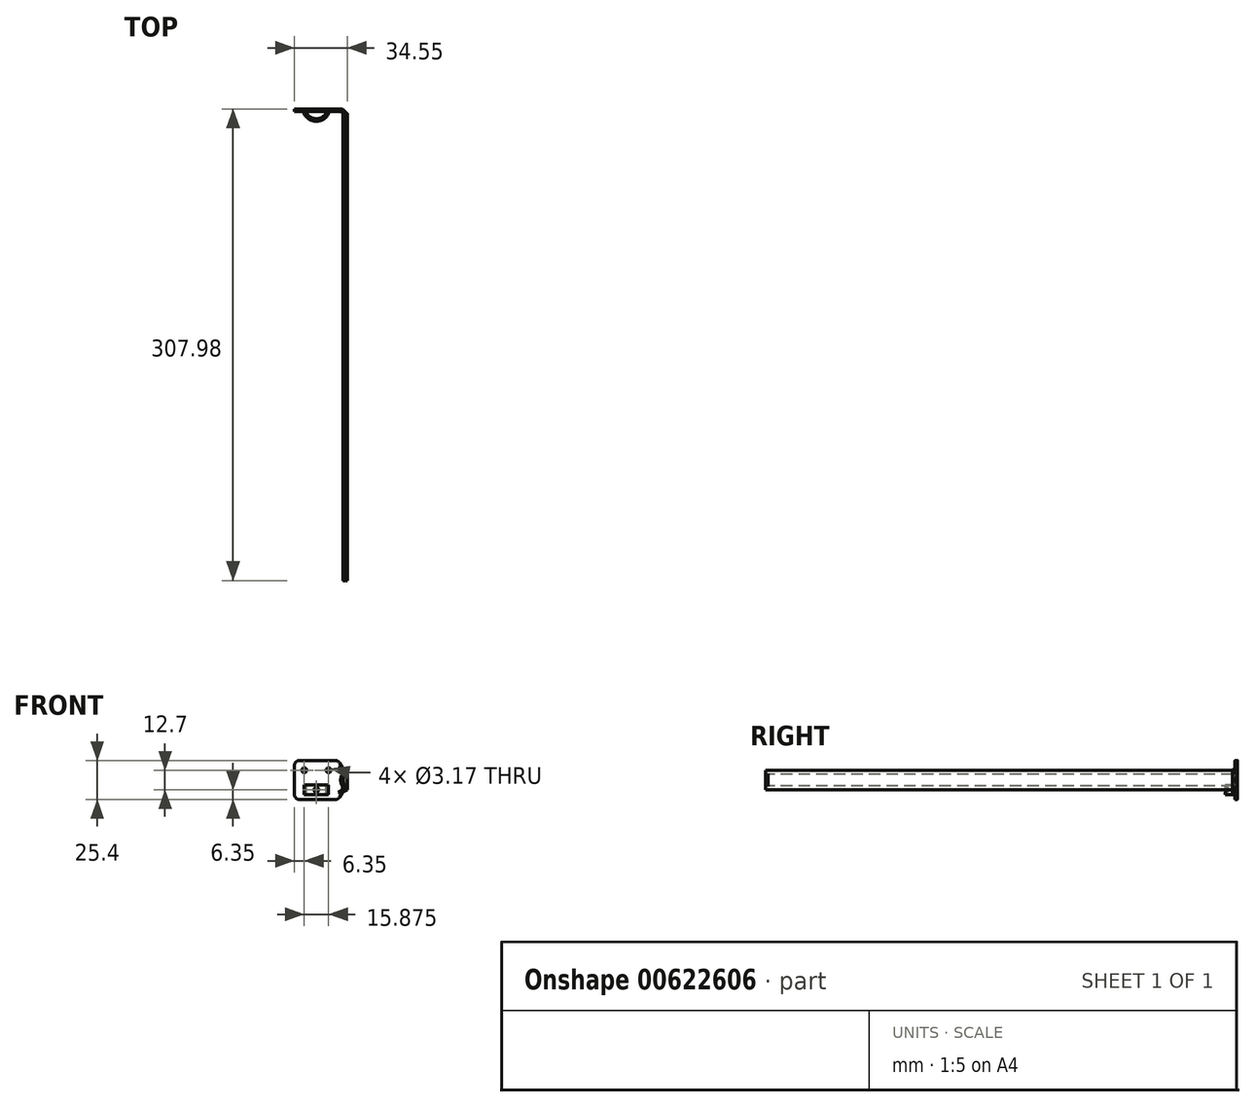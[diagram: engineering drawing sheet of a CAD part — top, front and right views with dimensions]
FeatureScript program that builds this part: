
annotation { "Feature Type Name" : "Feature", "Feature Type Description" : "" }
export const myFeature = defineFeature(function(context is Context, id is Id, definition is map)
    precondition{}
    {
        {
            var Q0;
            Q0=qCreatedBy(makeId("Front.planeOp"),FACE);
            var sketch = newSketch(context, id + "F0", { "sketchPlane" : qUnion([Q0])});
            skLineSegment(sketch, "E0", {"start": v(0, 6.35) * mm, "end": v(0, 4.22) * mm});
            skLineSegment(sketch, "E1", {"start": v(0, -6.35) * mm, "end": v(0, -4.22) * mm});
            skArc(sketch, "E2", {"start": v(-0.49, 2.53) * mm, "mid": v(-1.21, 0) * mm, "end": v(-0.49, -2.53) * mm});
            skPoint(sketch, "E3.visualSharp", {"position": v(0, 3.17) * mm});
            skArc(sketch, "E3.filletArc", {"start": v(-0.49, 2.53) * mm, "mid": v(-0.12, 3.34) * mm, "end": v(0, 4.22) * mm});
            skPoint(sketch, "E4.visualSharp", {"position": v(0, -3.18) * mm});
            skArc(sketch, "E4.filletArc", {"start": v(0, -4.22) * mm, "mid": v(-0.12, -3.34) * mm, "end": v(-0.49, -2.53) * mm});
            skLineSegment(sketch, "E5.0", {"start": v(-1.59, -6.35) * mm, "end": v(-1.59, -3.73) * mm});
            skArc(sketch, "E5.1", {"start": v(-1.59, 3.73) * mm, "mid": v(-2.8, 0) * mm, "end": v(-1.59, -3.73) * mm});
            skLineSegment(sketch, "E5.2", {"start": v(-1.59, 6.35) * mm, "end": v(-1.59, 3.73) * mm});
            skLineSegment(sketch, "E6", {"start": v(-1.59, 6.35) * mm, "end": v(0, 6.35) * mm});
            skLineSegment(sketch, "E7", {"start": v(-1.59, -6.35) * mm, "end": v(0, -6.35) * mm});
            skSolve(sketch);
        }
        {
            var Q0;
            Q0=qSketchRegion(id+"F0",true);
            extrude(context, id + "F1", {"entities" : qUnion([Q0]), "oppositeDirection" : true, "depth" : 304.8 * mm, "offsetDistance" : 25.4 * mm});
        }
        {
            var Q0;
            Q0=makeQuery(id+"F1.opExtrude","CAP_FACE",FACE,{"disambiguationData":[OSD([sQuery(id+"F0.wireOp",EDGE,"E0"),sQuery(id+"F0.wireOp",EDGE,"E1"),sQuery(id+"F0.wireOp",EDGE,"E2"),sQuery(id+"F0.wireOp",EDGE,"E3.filletArc"),sQuery(id+"F0.wireOp",EDGE,"E4.filletArc"),sQuery(id+"F0.wireOp",EDGE,"E5.0"),sQuery(id+"F0.wireOp",EDGE,"E5.1"),sQuery(id+"F0.wireOp",EDGE,"E5.2"),sQuery(id+"F0.wireOp",EDGE,"E6"),sQuery(id+"F0.wireOp",EDGE,"E7")])],"isStart":false});
            cPlane(context, id + "F2", {"entities" : qUnion([Q0]), "cplaneType" : CPlaneType.OFFSET, "offset" : 3.17 * mm, "width" : 152.4 * mm, "height" : 152.4 * mm});
        }
        {
            var Q0;
            Q0=qCreatedBy(id+"F2.planeOp",FACE);
            var sketch = newSketch(context, id + "F3", { "sketchPlane" : qUnion([Q0])});
            skLineSegment(sketch, "E8.0", {"start": v(4.76, -6.35) * mm, "end": v(4.76, -4.65) * mm});
            skArc(sketch, "E8.1", {"start": v(4.76, 4.65) * mm, "mid": v(5.98, 0) * mm, "end": v(4.76, -4.65) * mm});
            skLineSegment(sketch, "E8.2", {"start": v(4.76, 6.35) * mm, "end": v(4.76, 4.65) * mm});
            skLineSegment(sketch, "E9.0", {"start": v(3.18, -6.35) * mm, "end": v(3.18, -5.05) * mm});
            skArc(sketch, "E9.1", {"start": v(3.52, 3.6) * mm, "mid": v(4.39, 0) * mm, "end": v(3.52, -3.6) * mm});
            skLineSegment(sketch, "E9.2", {"start": v(3.18, 6.35) * mm, "end": v(3.18, 5.05) * mm});
            skLineSegment(sketch, "E10", {"start": v(3.18, 6.35) * mm, "end": v(4.76, 6.35) * mm});
            skLineSegment(sketch, "E11", {"start": v(3.18, -6.35) * mm, "end": v(4.76, -6.35) * mm});
            skPoint(sketch, "E12.visualSharp", {"position": v(3.18, 4.22) * mm});
            skArc(sketch, "E12.filletArc", {"start": v(3.18, 5.05) * mm, "mid": v(3.26, 4.3) * mm, "end": v(3.52, 3.6) * mm});
            skPoint(sketch, "E13.visualSharp", {"position": v(3.18, -4.22) * mm});
            skArc(sketch, "E13.filletArc", {"start": v(3.52, -3.6) * mm, "mid": v(3.26, -4.3) * mm, "end": v(3.18, -5.05) * mm});
            skLineSegment(sketch, "E14", {"start": v(5.98, 0) * mm, "end": v(5.98, 6.46) * mm, "construction": true});
            skLineSegment(sketch, "E15", {"start": v(5.98, 0) * mm, "end": v(5.98, -6.35) * mm, "construction": true});
            skSolve(sketch);
        }
        {
            var Q1;
            Q1=makeQuery(id+"F1.opExtrude","CAP_FACE",FACE,{"disambiguationData":[OSD([sQuery(id+"F0.wireOp",EDGE,"E0"),sQuery(id+"F0.wireOp",EDGE,"E1"),sQuery(id+"F0.wireOp",EDGE,"E2"),sQuery(id+"F0.wireOp",EDGE,"E3.filletArc"),sQuery(id+"F0.wireOp",EDGE,"E4.filletArc"),sQuery(id+"F0.wireOp",EDGE,"E5.0"),sQuery(id+"F0.wireOp",EDGE,"E5.1"),sQuery(id+"F0.wireOp",EDGE,"E5.2"),sQuery(id+"F0.wireOp",EDGE,"E6"),sQuery(id+"F0.wireOp",EDGE,"E7")])],"isStart":false});
            var Q2;
            Q2=makeQuery(id+"F3.imprint","IMPRINT",FACE,{"disambiguationData":[TD([[makeQuery(id+"F3.imprint","IMPRINT",EDGE,{"derivedFrom":sQuery(id+"F3.wireOp",EDGE,"E8.0")}),1.0]])]});
            loft(context, id + "F4", {"operationType" : NewBodyOperationType.ADD, "sheetProfilesArray" : [{ "sheetProfileEntities" : qUnion([Q1]) }, { "sheetProfileEntities" : qUnion([Q2]) }]});
        }
        {
            var Q0;
            Q0=makeQuery(id+"F4.opLoft","CAP_FACE",FACE,{"disambiguationData":[OSD([makeQuery(id+"F3.imprint","IMPRINT",FACE,{"disambiguationData":[TD([[makeQuery(id+"F3.imprint","IMPRINT",EDGE,{"derivedFrom":sQuery(id+"F3.wireOp",EDGE,"E8.0")}),1.0]])]})])],"isStart":true});
            cPlane(context, id + "F5", {"entities" : qUnion([Q0]), "cplaneType" : CPlaneType.OFFSET, "offset" : 0 * mm, "width" : 152.4 * mm, "height" : 152.4 * mm});
        }
        {
            var Q0;
            Q0=qCreatedBy(id+"F5.planeOp",FACE);
            var sketch = newSketch(context, id + "F6", { "sketchPlane" : qUnion([Q0])});
            skLineSegment(sketch, "E16.bottom", {"start": v(3.17, -7.94) * mm, "end": v(5.98, -7.94) * mm});
            skLineSegment(sketch, "E16.top", {"start": v(3.18, 7.94) * mm, "end": v(5.98, 7.94) * mm});
            skLineSegment(sketch, "E16.left", {"start": v(3.18, -7.94) * mm, "end": v(3.18, 7.94) * mm});
            skLineSegment(sketch, "E16.right", {"start": v(5.98, -7.94) * mm, "end": v(5.98, 7.94) * mm});
            skPoint(sketch, "E16.middle", {"position": v(4.58, 0) * mm});
            skLineSegment(sketch, "E17", {"start": v(4.58, 7.94) * mm, "end": v(4.58, -7.94) * mm, "construction": true});
            skSolve(sketch);
        }
        {
            var Q0;
            Q0=qSketchRegion(id+"F6",true);
            extrude(context, id + "F7", {"entities" : qUnion([Q0]), "operationType" : NewBodyOperationType.ADD, "oppositeDirection" : true, "depth" : 1.59 * mm, "offsetDistance" : 25.4 * mm});
        }
        {
            var Q0;
            {var subQ0=sQuery(id+"F0.wireOp",EDGE,"E6");Q0=makeQuery(id+"F4.boolean.opBoolean","MERGE",FACE,{"derivedFrom":[makeQuery(id+"F1.opExtrude","SWEPT_FACE",FACE,{"disambiguationData":[OSD([subQ0])]}),makeQuery(id+"F4.opLoft","SWEPT_FACE",FACE,{"disambiguationData":[OSD([sQuery(id+"F0.wireOp",EDGE,"E0"),sQuery(id+"F0.wireOp",EDGE,"E5.2"),subQ0,sQuery(id+"F3.wireOp",EDGE,"E8.2"),sQuery(id+"F3.wireOp",EDGE,"E9.2"),sQuery(id+"F3.wireOp",EDGE,"E10")])]})]});}
            var sketch = newSketch(context, id + "F8", { "sketchPlane" : qUnion([Q0])});
            skLineSegment(sketch, "E18", {"start": v(-1.59, 304.8) * mm, "end": v(0, 304.8) * mm});
            skSolve(sketch);
        }
        {
            var Q1;
            Q1=makeQuery(id+"F7.opExtrude","SWEPT_FACE",FACE,{"disambiguationData":[OSD([sQuery(id+"F6.wireOp",EDGE,"E16.top")])]});
            var Q2;
            Q2=makeQuery(id+"F8.imprint","IMPRINT",FACE,{"disambiguationData":[TD([[makeQuery(id+"F8.imprint","IMPRINT",EDGE,{"derivedFrom":sQuery(id+"F8.wireOp",EDGE,"E18")}),1.0]])]});
            loft(context, id + "F9", {"operationType" : NewBodyOperationType.ADD, "sheetProfilesArray" : [{ "sheetProfileEntities" : qUnion([Q1]) }, { "sheetProfileEntities" : qUnion([Q2]) }]});
        }
        {
            var Q0;
            {var subQ0=sQuery(id+"F0.wireOp",EDGE,"E7");Q0=makeQuery(id+"F4.boolean.opBoolean","MERGE",FACE,{"derivedFrom":[makeQuery(id+"F1.opExtrude","SWEPT_FACE",FACE,{"disambiguationData":[OSD([subQ0])]}),makeQuery(id+"F4.opLoft","SWEPT_FACE",FACE,{"disambiguationData":[OSD([sQuery(id+"F0.wireOp",EDGE,"E1"),sQuery(id+"F0.wireOp",EDGE,"E5.0"),subQ0,sQuery(id+"F3.wireOp",EDGE,"E8.0"),sQuery(id+"F3.wireOp",EDGE,"E9.0"),sQuery(id+"F3.wireOp",EDGE,"E11")])]})]});}
            var sketch = newSketch(context, id + "F10", { "sketchPlane" : qUnion([Q0])});
            skLineSegment(sketch, "E19", {"start": v(0, -304.8) * mm, "end": v(-1.59, -304.8) * mm});
            skSolve(sketch);
        }
        {
            var Q1;
            Q1=makeQuery(id+"F7.opExtrude","SWEPT_FACE",FACE,{"disambiguationData":[OSD([sQuery(id+"F6.wireOp",EDGE,"E16.bottom")])]});
            var Q2;
            Q2=makeQuery(id+"F10.imprint","IMPRINT",FACE,{"disambiguationData":[TD([[makeQuery(id+"F10.imprint","IMPRINT",EDGE,{"derivedFrom":sQuery(id+"F10.wireOp",EDGE,"E19")}),1.0]])]});
            loft(context, id + "F11", {"operationType" : NewBodyOperationType.ADD, "sheetProfilesArray" : [{ "sheetProfileEntities" : qUnion([Q1]) }, { "sheetProfileEntities" : qUnion([Q2]) }]});
        }
        {
            var Q0;
            Q0=makeQuery(id+"F7.opExtrude","SWEPT_FACE",FACE,{"disambiguationData":[OSD([sQuery(id+"F6.wireOp",EDGE,"E16.right")])]});
            var sketch = newSketch(context, id + "F12", { "sketchPlane" : qUnion([Q0])});
            skLineSegment(sketch, "E20.bottom", {"start": v(-307.98, -12.7) * mm, "end": v(-306.39, -12.7) * mm});
            skLineSegment(sketch, "E20.top", {"start": v(-307.98, 12.7) * mm, "end": v(-306.39, 12.7) * mm});
            skLineSegment(sketch, "E20.left", {"start": v(-307.98, -12.7) * mm, "end": v(-307.98, 12.7) * mm});
            skLineSegment(sketch, "E20.right", {"start": v(-306.39, -12.7) * mm, "end": v(-306.39, 12.7) * mm});
            skPoint(sketch, "E20.middle", {"position": v(-307.18, 0) * mm});
            skPoint(sketch, "E20.middle.positionSnap0", {"position": v(-307.18, 7.94) * mm});
            skPoint(sketch, "E20.middle.positionSnap1", {"position": v(-306.39, 0) * mm});
            skPoint(sketch, "E20.centerSnap0", {"position": v(-307.18, 7.94) * mm});
            skPoint(sketch, "E20.centerSnap1", {"position": v(-306.39, 0) * mm});
            skSolve(sketch);
        }
        {
            var Q0;
            Q0=qSketchRegion(id+"F12",true);
            extrude(context, id + "F13", {"entities" : qUnion([Q0]), "operationType" : NewBodyOperationType.ADD, "depth" : 28.57 * mm, "offsetDistance" : 25.4 * mm});
        }
        {
            var Q1;
            Q1=makeQuery(id+"F7.opExtrude","SWEPT_FACE",FACE,{"disambiguationData":[OSD([sQuery(id+"F6.wireOp",EDGE,"E16.top")])]});
            var Q2;
            Q2=makeQuery(id+"F13.opExtrude","SWEPT_FACE",FACE,{"disambiguationData":[OSD([sQuery(id+"F12.wireOp",EDGE,"E20.top")])]});
            loft(context, id + "F14", {"operationType" : NewBodyOperationType.ADD, "sheetProfilesArray" : [{ "sheetProfileEntities" : qUnion([Q1]) }, { "sheetProfileEntities" : qUnion([Q2]) }]});
        }
        {
            var Q1;
            Q1=makeQuery(id+"F7.opExtrude","SWEPT_FACE",FACE,{"disambiguationData":[OSD([sQuery(id+"F6.wireOp",EDGE,"E16.bottom")])]});
            var Q2;
            Q2=makeQuery(id+"F13.opExtrude","SWEPT_FACE",FACE,{"disambiguationData":[OSD([sQuery(id+"F12.wireOp",EDGE,"E20.bottom")])]});
            loft(context, id + "F15", {"operationType" : NewBodyOperationType.ADD, "sheetProfilesArray" : [{ "sheetProfileEntities" : qUnion([Q1]) }, { "sheetProfileEntities" : qUnion([Q2]) }]});
        }
        {
            var Q0;
            {var subQ0=sQuery(id+"F12.wireOp",EDGE,"E20.right");var subQ1=sQuery(id+"F6.wireOp",EDGE,"E16.right");var subQ2=sQuery(id+"F6.wireOp",EDGE,"E16.left");var subQ3=sQuery(id+"F6.wireOp",EDGE,"E16.bottom");var subQ4=sQuery(id+"F6.wireOp",EDGE,"E16.top");Q0=makeQuery(id+"F15.boolean.opBoolean","MERGE",FACE,{"derivedFrom":[makeQuery(id+"F14.boolean.opBoolean","MERGE",FACE,{"derivedFrom":[makeQuery(id+"F13.boolean.opBoolean","MERGE",FACE,{"derivedFrom":[makeQuery(id+"F7.opExtrude","CAP_FACE",FACE,{"disambiguationData":[OSD([subQ3,subQ4,subQ2,subQ1])],"isStart":false}),makeQuery(id+"F13.opExtrude","SWEPT_FACE",FACE,{"disambiguationData":[OSD([subQ0])]})]}),makeQuery(id+"F14.opLoft","SWEPT_FACE",FACE,{"disambiguationData":[OSD([subQ4,subQ2,subQ1,sQuery(id+"F12.wireOp",EDGE,"E20.top"),subQ0])]})]}),makeQuery(id+"F15.opLoft","SWEPT_FACE",FACE,{"disambiguationData":[OSD([subQ3,subQ2,subQ1,sQuery(id+"F12.wireOp",EDGE,"E20.bottom"),subQ0])]})]});}
            var sketch = newSketch(context, id + "F16", { "sketchPlane" : qUnion([Q0])});
            skLineSegment(sketch, "E21", {"start": v(-28.2, 12.7) * mm, "end": v(-28.2, -12.7) * mm, "construction": true});
            skCircle(sketch, "E22", {"center": v(-28.2, 6.35) * mm, "radius": 1.59 * mm});
            skLineSegment(sketch, "E23", {"start": v(-28.2, 6.35) * mm, "end": v(-12.33, 6.35) * mm, "construction": true});
            skCircle(sketch, "E24", {"center": v(-12.33, 6.35) * mm, "radius": 1.59 * mm});
            skSolve(sketch);
        }
        {
            var Q0;
            Q0=qSketchRegion(id+"F16",true);
            extrude(context, id + "F17", {"entities" : qUnion([Q0]), "operationType" : NewBodyOperationType.REMOVE, "oppositeDirection" : true, "depth" : 25.4 * mm, "offsetDistance" : 25.4 * mm});
        }
        {
            var Q0;
            {var subQ0=sQuery(id+"F12.wireOp",EDGE,"E20.right");var subQ1=sQuery(id+"F6.wireOp",EDGE,"E16.right");var subQ2=sQuery(id+"F6.wireOp",EDGE,"E16.left");var subQ3=sQuery(id+"F6.wireOp",EDGE,"E16.bottom");var subQ4=sQuery(id+"F6.wireOp",EDGE,"E16.top");Q0=makeQuery(id+"F15.boolean.opBoolean","MERGE",FACE,{"derivedFrom":[makeQuery(id+"F14.boolean.opBoolean","MERGE",FACE,{"derivedFrom":[makeQuery(id+"F13.boolean.opBoolean","MERGE",FACE,{"derivedFrom":[makeQuery(id+"F7.opExtrude","CAP_FACE",FACE,{"disambiguationData":[OSD([subQ3,subQ4,subQ2,subQ1])],"isStart":false}),makeQuery(id+"F13.opExtrude","SWEPT_FACE",FACE,{"disambiguationData":[OSD([subQ0])]})]}),makeQuery(id+"F14.opLoft","SWEPT_FACE",FACE,{"disambiguationData":[OSD([subQ4,subQ2,subQ1,sQuery(id+"F12.wireOp",EDGE,"E20.top"),subQ0])]})]}),makeQuery(id+"F15.opLoft","SWEPT_FACE",FACE,{"disambiguationData":[OSD([subQ3,subQ2,subQ1,sQuery(id+"F12.wireOp",EDGE,"E20.bottom"),subQ0])]})]});}
            var sketch = newSketch(context, id + "F18", { "sketchPlane" : qUnion([Q0])});
            skLineSegment(sketch, "E25", {"start": v(-20.26, -12.7) * mm, "end": v(-20.26, 12.7) * mm, "construction": true});
            skLineSegment(sketch, "E26.bottom", {"start": v(-28.2, -9.53) * mm, "end": v(-12.33, -9.53) * mm});
            skLineSegment(sketch, "E26.top", {"start": v(-28.2, -3.18) * mm, "end": v(-12.33, -3.18) * mm});
            skLineSegment(sketch, "E26.left", {"start": v(-28.2, -9.53) * mm, "end": v(-28.2, -3.18) * mm});
            skLineSegment(sketch, "E26.right", {"start": v(-12.33, -9.53) * mm, "end": v(-12.33, -3.18) * mm});
            skPoint(sketch, "E26.middle", {"position": v(-20.26, -6.35) * mm});
            skSolve(sketch);
        }
        {
            var Q0;
            Q0=qSketchRegion(id+"F18",true);
            extrude(context, id + "F19", {"entities" : qUnion([Q0]), "operationType" : NewBodyOperationType.ADD, "depth" : 6.35 * mm, "offsetDistance" : 25.4 * mm});
        }
        {
            var Q0;
            Q0=makeQuery(id+"F19.opExtrude","SWEPT_FACE",FACE,{"disambiguationData":[OSD([sQuery(id+"F18.wireOp",EDGE,"E26.top")])]});
            var sketch = newSketch(context, id + "F20", { "sketchPlane" : qUnion([Q0])});
            skLineSegment(sketch, "E27", {"start": v(-20.26, 306.39) * mm, "end": v(-20.26, 300.04) * mm, "construction": true});
            skLineSegment(sketch, "E28", {"start": v(-28.2, 303.21) * mm, "end": v(-12.33, 303.21) * mm, "construction": true});
            skLineSegment(sketch, "E29", {"start": v(-28.2, 304.8) * mm, "end": v(-12.33, 304.8) * mm, "construction": true});
            skLineSegment(sketch, "E30", {"start": v(-26.61, 306.39) * mm, "end": v(-26.61, 306.23) * mm});
            skLineSegment(sketch, "E31", {"start": v(-13.91, 306.39) * mm, "end": v(-13.91, 306.23) * mm});
            skArc(sketch, "E32", {"start": v(-28.2, 304.8) * mm, "mid": v(-20.26, 300.04) * mm, "end": v(-12.33, 304.8) * mm});
            skArc(sketch, "E33.0", {"start": v(-25.82, 304.13) * mm, "mid": v(-20.26, 301.62) * mm, "end": v(-14.7, 304.13) * mm});
            skPoint(sketch, "E34.visualSharp", {"position": v(-26.61, 305.22) * mm});
            skArc(sketch, "E34.filletArc", {"start": v(-26.61, 306.23) * mm, "mid": v(-26.4, 305.11) * mm, "end": v(-25.82, 304.13) * mm});
            skPoint(sketch, "E35.visualSharp", {"position": v(-13.91, 305.22) * mm});
            skArc(sketch, "E35.filletArc", {"start": v(-14.7, 304.13) * mm, "mid": v(-14.12, 305.11) * mm, "end": v(-13.91, 306.23) * mm});
            skSolve(sketch);
        }
        {
            var Q0;
            Q0=qSketchRegion(id+"F20",true);
            var Q1;
            {var subQ0=sQuery(id+"F20.wireOp",EDGE,"E32");var subQ1=sQuery(id+"F18.wireOp",EDGE,"E26.top");var subQ4=makeQuery(id+"F19.opExtrude","CAP_EDGE",EDGE,{"disambiguationData":[OSD([subQ1])],"isStart":false});var subQ5=makeQuery(id+"F20.imprint","INTERSECT",VERTEX,{"derivedFrom":[subQ4,subQ0]});Q1=makeQuery(id+"F20.imprint","IMPRINT",FACE,{"disambiguationData":[TD([[makeQuery(id+"F20.imprint","IMPRINT",EDGE,{"disambiguationData":[TD([[subQ5,1.0]])],"derivedFrom":subQ0}),-1.0]])]});}
            var Q2;
            {var subQ0=sQuery(id+"F20.wireOp",EDGE,"E32");var subQ1=sQuery(id+"F18.wireOp",EDGE,"E26.top");var subQ4=makeQuery(id+"F19.opExtrude","CAP_EDGE",EDGE,{"disambiguationData":[OSD([subQ1])],"isStart":false});var subQ5=makeQuery(id+"F20.imprint","INTERSECT",VERTEX,{"derivedFrom":[subQ4,subQ0]});Q2=makeQuery(id+"F20.imprint","IMPRINT",FACE,{"disambiguationData":[TD([[makeQuery(id+"F20.imprint","IMPRINT",EDGE,{"disambiguationData":[TD([[subQ5,-1.0]])],"derivedFrom":subQ0}),-1.0]])]});}
            var Q3;
            {var subQ0=sQuery(id+"F20.wireOp",EDGE,"E30");Q3=makeQuery(id+"F20.imprint","IMPRINT",FACE,{"disambiguationData":[TD([[makeQuery(id+"F20.imprint","IMPRINT",EDGE,{"derivedFrom":subQ0}),1.0]])]});}
            extrude(context, id + "F21", {"entities" : qUnion([Q0, Q1, Q2, Q3]), "operationType" : NewBodyOperationType.REMOVE, "oppositeDirection" : true, "depth" : 25.4 * mm, "offsetDistance" : 25.4 * mm});
        }
        {
            var Q0;
            {var subQ0=sQuery(id+"F12.wireOp",EDGE,"E20.left");var subQ1=sQuery(id+"F6.wireOp",EDGE,"E16.right");var subQ2=sQuery(id+"F6.wireOp",EDGE,"E16.left");var subQ3=sQuery(id+"F6.wireOp",EDGE,"E16.bottom");var subQ4=sQuery(id+"F6.wireOp",EDGE,"E16.top");Q0=makeQuery(id+"F15.boolean.opBoolean","MERGE",FACE,{"derivedFrom":[makeQuery(id+"F14.boolean.opBoolean","MERGE",FACE,{"derivedFrom":[makeQuery(id+"F13.boolean.opBoolean","MERGE",FACE,{"derivedFrom":[makeQuery(id+"F7.boolean.opBoolean","MERGE",FACE,{"derivedFrom":[makeQuery(id+"F4.opLoft","CAP_FACE",FACE,{"disambiguationData":[OSD([makeQuery(id+"F3.imprint","IMPRINT",FACE,{"disambiguationData":[TD([[makeQuery(id+"F3.imprint","IMPRINT",EDGE,{"derivedFrom":sQuery(id+"F3.wireOp",EDGE,"E8.0")}),1.0]])]})])],"isStart":true}),makeQuery(id+"F7.opExtrude","CAP_FACE",FACE,{"disambiguationData":[OSD([subQ3,subQ4,subQ2,subQ1])],"isStart":true})]}),makeQuery(id+"F13.opExtrude","SWEPT_FACE",FACE,{"disambiguationData":[OSD([subQ0])]})]}),makeQuery(id+"F14.opLoft","SWEPT_FACE",FACE,{"disambiguationData":[OSD([subQ4,subQ2,subQ1,sQuery(id+"F12.wireOp",EDGE,"E20.top"),subQ0])]})]}),makeQuery(id+"F15.opLoft","SWEPT_FACE",FACE,{"disambiguationData":[OSD([subQ3,subQ2,subQ1,sQuery(id+"F12.wireOp",EDGE,"E20.bottom"),subQ0])]})]});}
            var sketch = newSketch(context, id + "F22", { "sketchPlane" : qUnion([Q0])});
            skLineSegment(sketch, "E36", {"start": v(20.26, -12.7) * mm, "end": v(20.26, 12.7) * mm, "construction": true});
            skLineSegment(sketch, "E37", {"start": v(34.55, -6.35) * mm, "end": v(3.18, -6.35) * mm, "construction": true});
            skCircle(sketch, "E38", {"center": v(20.26, -6.35) * mm, "radius": 1.59 * mm});
            skSolve(sketch);
        }
        {
            var Q0;
            Q0=qSketchRegion(id+"F22",true);
            extrude(context, id + "F23", {"entities" : qUnion([Q0]), "operationType" : NewBodyOperationType.REMOVE, "oppositeDirection" : true, "depth" : 25.4 * mm, "offsetDistance" : 25.4 * mm});
        }
        {
            var Q0;
            Q0=makeQuery(id+"F1.opExtrude","CAP_FACE",FACE,{"disambiguationData":[OSD([sQuery(id+"F0.wireOp",EDGE,"E0"),sQuery(id+"F0.wireOp",EDGE,"E1"),sQuery(id+"F0.wireOp",EDGE,"E2"),sQuery(id+"F0.wireOp",EDGE,"E3.filletArc"),sQuery(id+"F0.wireOp",EDGE,"E4.filletArc"),sQuery(id+"F0.wireOp",EDGE,"E5.0"),sQuery(id+"F0.wireOp",EDGE,"E5.1"),sQuery(id+"F0.wireOp",EDGE,"E5.2"),sQuery(id+"F0.wireOp",EDGE,"E6"),sQuery(id+"F0.wireOp",EDGE,"E7")])],"isStart":true});
            var sketch = newSketch(context, id + "F24", { "sketchPlane" : qUnion([Q0])});
            skLineSegment(sketch, "E39", {"start": v(0, 4.22) * mm, "end": v(0, -4.22) * mm, "construction": true});
            skLineSegment(sketch, "E40", {"start": v(-1.21, 0) * mm, "end": v(-1.21, 3.34) * mm, "construction": true});
            skLineSegment(sketch, "E41", {"start": v(-1.21, 0) * mm, "end": v(-1.21, -3.34) * mm, "construction": true});
            skLineSegment(sketch, "E42", {"start": v(-1.21, 2.53) * mm, "end": v(-0.49, 2.53) * mm, "construction": true});
            skLineSegment(sketch, "E43", {"start": v(-1.21, -2.53) * mm, "end": v(0, -2.53) * mm, "construction": true});
            skLineSegment(sketch, "E44", {"start": v(-0.49, 2.53) * mm, "end": v(0, 2.53) * mm, "construction": true});
            skPoint(sketch, "E45", {"position": v(-0.12, 3.34) * mm});
            skPoint(sketch, "E46", {"position": v(-0.12, -3.34) * mm});
            skLineSegment(sketch, "E47", {"start": v(0, 4.22) * mm, "end": v(0, -4.22) * mm});
            skArc(sketch, "E48", {"start": v(-0.49, 2.53) * mm, "mid": v(-1.21, 0) * mm, "end": v(-0.49, -2.53) * mm});
            skArc(sketch, "E49", {"start": v(-0.49, 2.53) * mm, "mid": v(-0.12, 3.34) * mm, "end": v(0, 4.22) * mm});
            skArc(sketch, "E50", {"start": v(0, -4.22) * mm, "mid": v(-0.12, -3.34) * mm, "end": v(-0.49, -2.53) * mm});
            skSolve(sketch);
        }
        {
            var Q0;
            Q0=qSketchRegion(id+"F24",true);
            extrude(context, id + "F25", {"entities" : qUnion([Q0]), "operationType" : NewBodyOperationType.ADD, "oppositeDirection" : true, "depth" : 1.59 * mm, "offsetDistance" : 25.4 * mm});
        }
        {
            var Q0;
            Q0=makeQuery(id+"F13.opExtrude","CAP_EDGE",EDGE,{"disambiguationData":[OSD([sQuery(id+"F12.wireOp",EDGE,"E20.top")])],"isStart":false});
            var Q1;
            Q1=makeQuery(id+"F13.opExtrude","CAP_EDGE",EDGE,{"disambiguationData":[OSD([sQuery(id+"F12.wireOp",EDGE,"E20.bottom")])],"isStart":false});
            fillet(context, id + "F26", {"entities" : qUnion([Q0, Q1]), "radius" : 3.17 * mm, "tangentPropagation" : true, "allowEdgeOverflow" : false});
        }
        {
            var Q0;
            {var subQ0=sQuery(id+"F12.wireOp",EDGE,"E20.top");var subQ1=makeQuery(id+"F13.opExtrude","CAP_EDGE",EDGE,{"disambiguationData":[OSD([subQ0])],"isStart":true});var subQ2=sQuery(id+"F12.wireOp",EDGE,"E20.right");var subQ3=sQuery(id+"F12.wireOp",EDGE,"E20.left");Q0=makeQuery(id+"F14.boolean.opBoolean","MERGE",EDGE,{"derivedFrom":[subQ1,makeQuery(id+"F14.opLoft","MID_CAP_EDGE",EDGE,{"disambiguationData":[OSD([subQ0,subQ3,subQ2]),TDD([makeQuery(id+"F13.opExtrude","CAP_VERTEX",VERTEX,{"disambiguationData":[OSD([subQ0,subQ3])],"isStart":true}),makeQuery(id+"F13.opExtrude","CAP_VERTEX",VERTEX,{"disambiguationData":[OSD([subQ0,subQ2])],"isStart":true}),subQ1])],"capPos":1.0})]});}
            fillet(context, id + "F27", {"entities" : qUnion([Q0]), "radius" : 3.17 * mm, "tangentPropagation" : true, "allowEdgeOverflow" : false});
        }
        {
            var Q0;
            {var subQ0=sQuery(id+"F12.wireOp",EDGE,"E20.bottom");var subQ1=makeQuery(id+"F13.opExtrude","CAP_EDGE",EDGE,{"disambiguationData":[OSD([subQ0])],"isStart":true});var subQ2=sQuery(id+"F12.wireOp",EDGE,"E20.right");var subQ3=sQuery(id+"F12.wireOp",EDGE,"E20.left");Q0=makeQuery(id+"F15.boolean.opBoolean","MERGE",EDGE,{"derivedFrom":[subQ1,makeQuery(id+"F15.opLoft","MID_CAP_EDGE",EDGE,{"disambiguationData":[OSD([subQ0,subQ3,subQ2]),TDD([makeQuery(id+"F13.opExtrude","CAP_VERTEX",VERTEX,{"disambiguationData":[OSD([subQ0,subQ3])],"isStart":true}),makeQuery(id+"F13.opExtrude","CAP_VERTEX",VERTEX,{"disambiguationData":[OSD([subQ0,subQ2])],"isStart":true}),subQ1])],"capPos":1.0})]});}
            fillet(context, id + "F28", {"entities" : qUnion([Q0]), "radius" : 3.17 * mm, "tangentPropagation" : true, "allowEdgeOverflow" : false});
        }
    });
